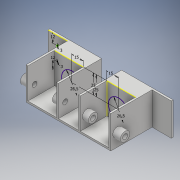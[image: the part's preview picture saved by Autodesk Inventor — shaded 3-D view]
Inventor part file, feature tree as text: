
AUTODESK INVENTOR PART (.ipt)
format: ipt  version: 2018.2 (Build 222227000, 227)  size: 217,088 bytes
history: native  units: mm
features: sketch x12, extrude x10
ambient origin geometry x8: Origin, YZ Plane, XZ Plane, XY Plane, X Axis, Y Axis, Z Axis, Center Point
bodies: Solid1 (feature_tree)
feature tree (22):
  extrude  "Extrusion1"  Depth=56.0mm
  extrude  "Extrusion2"  Depth=2.4mm
  extrude  "Extrusion3"  Depth=2.4mm
  extrude  "Extrusion4"  Depth=2.4mm
  sketch  "Sketch5"  dims[d9=2.4mm d10=39.6mm d11=0.0mm]
  extrude  "Extrusion5"  Depth=39.6mm TaperAngle=0.0deg
  extrude  "Extrusion6"  Depth=13.0mm
  extrude  "Extrusion7"  Depth=2.4mm
  extrude  "Extrusion8"  Depth=39.6mm TaperAngle=0.0deg
  extrude  "Extrusion9"  Depth=3.0mm
  extrude  "Extrusion10"  Depth=12.0mm
  sketch  "Sketch12"  dims[d26=6.3mm d27=17.0mm d28=45.0mm d29=110.0mm d30=0.0mm d31=12.0mm d32=10.0mm d33=0.0mm d34=12.0mm d35=8.0mm d36=0.0mm d37=12.0mm d38=10.0mm d39=0.0mm d40=12.0mm d41=8.0mm d42=0.0mm d43=26.5mm d44=26.5mm d45=15.0mm d46=15.0mm d47=25.0mm d48=25.0mm]
  sketch  "Sketch1"  dims[d0=110.0mm d1=56.0mm]
  sketch  "Sketch2"  dims[d2=25.0mm d3=2.4mm]
  sketch  "Sketch3"  dims[d4=25.0mm d5=2.4mm]
  sketch  "Sketch4"  dims[d6=42.0mm d7=0.0mm d8=2.4mm]
  sketch  "Sketch6"  dims[d12=13.0mm d13=13.0mm]
  sketch  "Sketch7"  dims[d14=39.6mm d15=0.0mm d16=2.4mm]
  sketch  "Sketch8"  dims[d17=2.4mm d18=39.6mm d19=0.0mm]
  sketch  "Sketch9"  dims[d20=3.0mm d21=3.0mm]
  sketch  "Sketch10"  dims[d22=12.0mm d23=12.0mm]
  sketch  "Sketch11"  dims[d24=19.0mm d25=0.0mm]
